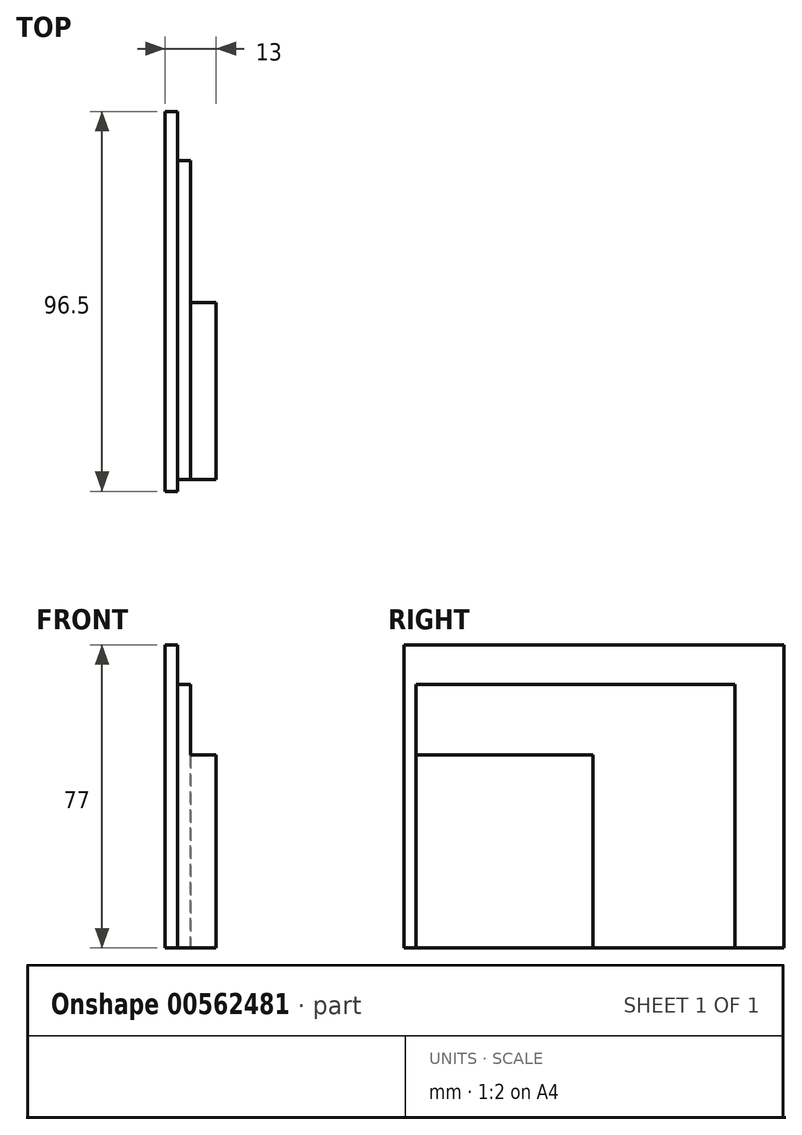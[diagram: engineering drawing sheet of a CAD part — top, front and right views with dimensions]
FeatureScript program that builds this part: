
annotation { "Feature Type Name" : "Feature", "Feature Type Description" : "" }
export const myFeature = defineFeature(function(context is Context, id is Id, definition is map)
    precondition{}
    {
        {
            var Q0;
            Q0=qCreatedBy(makeId("Right.planeOp"),FACE);
            var sketch = newSketch(context, id + "F0", { "sketchPlane" : qUnion([Q0])});
            skLineSegment(sketch, "E0.bottom", {"start": v(-48.25, 38.5) * mm, "end": v(48.25, 38.5) * mm});
            skLineSegment(sketch, "E0.top", {"start": v(-48.25, -38.5) * mm, "end": v(48.25, -38.5) * mm});
            skLineSegment(sketch, "E0.left", {"start": v(-48.25, 38.5) * mm, "end": v(-48.25, -38.5) * mm});
            skLineSegment(sketch, "E0.right", {"start": v(48.25, 38.5) * mm, "end": v(48.25, -38.5) * mm});
            skPoint(sketch, "E0.middle", {"position": v(0, 0) * mm});
            skSolve(sketch);
        }
        {
            var Q0;
            Q0=qSketchRegion(id+"F0",true);
            extrude(context, id + "F1", {"entities" : qUnion([Q0]), "depth" : 3.2 * mm, "offsetDistance" : 25 * mm, "symmetric" : true});
        }
        {
            var Q0;
            Q0=makeQuery(id+"F1.opExtrude","CAP_FACE",FACE,{"disambiguationData":[OSD([sQuery(id+"F0.wireOp",EDGE,"E0.bottom"),sQuery(id+"F0.wireOp",EDGE,"E0.top"),sQuery(id+"F0.wireOp",EDGE,"E0.left"),sQuery(id+"F0.wireOp",EDGE,"E0.right")])],"isStart":false});
            var sketch = newSketch(context, id + "F2", { "sketchPlane" : qUnion([Q0])});
            skLineSegment(sketch, "E1.bottom", {"start": v(-45.25, 28.5) * mm, "end": v(35.75, 28.5) * mm});
            skLineSegment(sketch, "E1.top", {"start": v(-45.25, -38.5) * mm, "end": v(35.75, -38.5) * mm});
            skLineSegment(sketch, "E1.left", {"start": v(-45.25, 28.5) * mm, "end": v(-45.25, -38.5) * mm});
            skLineSegment(sketch, "E1.right", {"start": v(35.75, 28.5) * mm, "end": v(35.75, -38.5) * mm});
            skSolve(sketch);
        }
        {
            var Q0;
            Q0=makeQuery(id+"F2.imprint","IMPRINT",FACE,{"disambiguationData":[TD([[makeQuery(id+"F2.imprint","IMPRINT",EDGE,{"derivedFrom":sQuery(id+"F2.wireOp",EDGE,"E1.bottom")}),-1.0]])]});
            extrude(context, id + "F3", {"entities" : qUnion([Q0]), "operationType" : NewBodyOperationType.ADD, "depth" : 3.3 * mm, "offsetDistance" : 25 * mm});
        }
        {
            var Q0;
            Q0=makeQuery(id+"F3.opExtrude","CAP_FACE",FACE,{"disambiguationData":[OSD([sQuery(id+"F2.wireOp",EDGE,"E1.bottom"),sQuery(id+"F2.wireOp",EDGE,"E1.top"),sQuery(id+"F2.wireOp",EDGE,"E1.left"),sQuery(id+"F2.wireOp",EDGE,"E1.right")])],"isStart":false});
            var sketch = newSketch(context, id + "F4", { "sketchPlane" : qUnion([Q0])});
            skLineSegment(sketch, "E2.bottom", {"start": v(-45.25, -38.5) * mm, "end": v(-0.25, -38.5) * mm});
            skLineSegment(sketch, "E2.top", {"start": v(-45.25, 10.5) * mm, "end": v(-0.25, 10.5) * mm});
            skLineSegment(sketch, "E2.left", {"start": v(-45.25, -38.5) * mm, "end": v(-45.25, 10.5) * mm});
            skLineSegment(sketch, "E2.right", {"start": v(-0.25, -38.5) * mm, "end": v(-0.25, 10.5) * mm});
            skSolve(sketch);
        }
        {
            var Q0;
            Q0 = qSketchRegion(id + "F4", true);
            extrude(context, id + "F5", {"entities" : qUnion([Q0]), "operationType" : NewBodyOperationType.ADD, "depth" : 6.5 * mm, "offsetDistance" : 25 * mm});
        }
    });
